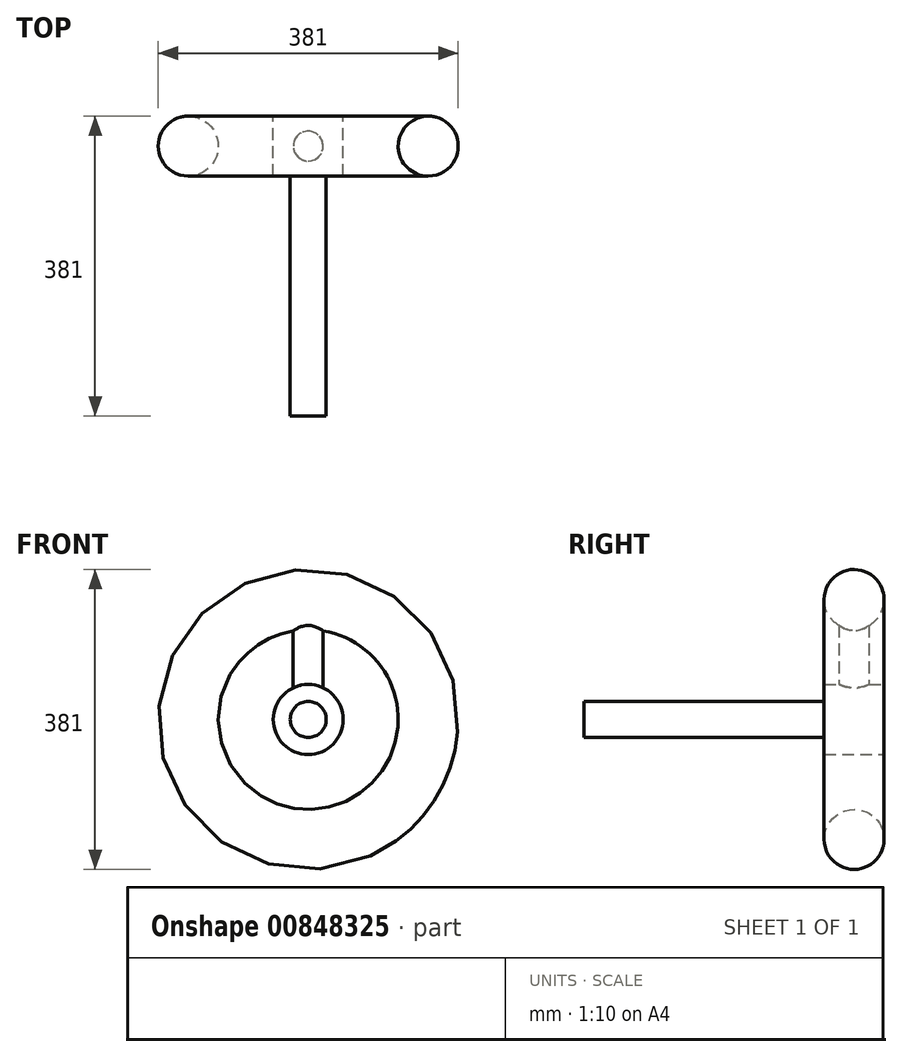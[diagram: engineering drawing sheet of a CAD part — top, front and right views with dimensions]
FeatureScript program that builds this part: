
annotation { "Feature Type Name" : "Feature", "Feature Type Description" : "" }
export const myFeature = defineFeature(function(context is Context, id is Id, definition is map)
    precondition{}
    {
        {
            var Q0;
            Q0=qCreatedBy(makeId("Right.planeOp"),FACE);
            var sketch = newSketch(context, id + "F0", { "sketchPlane" : qUnion([Q0])});
            skCircle(sketch, "E0", {"center": v(0, 152.4) * mm, "radius": 38.1 * mm});
            skLineSegment(sketch, "E1", {"start": v(-136.6, 0) * mm, "end": v(132.64, 0) * mm});
            skSolve(sketch);
        }
        {
            var Q0;
            Q0=makeQuery(id+"F0.imprint","IMPRINT",FACE,{"disambiguationData":[TD([[makeQuery(id+"F0.imprint","IMPRINT",EDGE,{"derivedFrom":sQuery(id+"F0.wireOp",EDGE,"E0")}),1.0]])]});
            var Q1;
            Q1=sQuery(id+"F0.wireOp",EDGE,"E1");
            revolve(context, id + "F1", {"surfaceOperationType" : NewSurfaceOperationType.NEW, "entities" : qUnion([Q0]), "axis" : qUnion([Q1]), "revolveType" : RevolveType.FULL});
        }
        {
            var Q0;
            Q0=qCreatedBy(makeId("Front.planeOp"),FACE);
            cPlane(context, id + "F2", {"entities" : qUnion([Q0]), "cplaneType" : CPlaneType.OFFSET, "offset" : 38.1 * mm, "oppositeDirection" : true, "width" : 152.4 * mm, "height" : 152.4 * mm});
        }
        {
            var Q0;
            Q0=qCreatedBy(id+"F2.planeOp",FACE);
            var sketch = newSketch(context, id + "F3", { "sketchPlane" : qUnion([Q0])});
            skCircle(sketch, "E2", {"center": v(0, 0) * mm, "radius": 44.45 * mm});
            skSolve(sketch);
        }
        {
            var Q0;
            Q0=makeQuery(id+"F3.imprint","IMPRINT",FACE,{"disambiguationData":[TD([[makeQuery(id+"F3.imprint","IMPRINT",EDGE,{"derivedFrom":sQuery(id+"F3.wireOp",EDGE,"E2")}),1.0]])]});
            extrude(context, id + "F4", {"entities" : qUnion([Q0]), "depth" : 76.2 * mm, "offsetDistance" : 25.4 * mm});
        }
        {
            var Q0;
            Q0=qCreatedBy(makeId("Top.planeOp"),FACE);
            cPlane(context, id + "F5", {"entities" : qUnion([Q0]), "cplaneType" : CPlaneType.OFFSET, "offset" : 38.1 * mm, "width" : 152.4 * mm, "height" : 152.4 * mm});
        }
        {
            var Q0;
            Q0=qCreatedBy(id+"F5.planeOp",FACE);
            var sketch = newSketch(context, id + "F6", { "sketchPlane" : qUnion([Q0])});
            skCircle(sketch, "E3", {"center": v(0, 0) * mm, "radius": 19.05 * mm});
            skSolve(sketch);
        }
        {
            var Q0;
            Q0 = qSketchRegion(id + "F6", true);
            var Q1;
            Q1=makeQuery(id+"F1.opRevolve","SWEPT_FACE",FACE,{"disambiguationData":[OSD([sQuery(id+"F0.wireOp",EDGE,"E0")])]});
            extrude(context, id + "F7", {"entities" : qUnion([Q0]), "operationType" : NewBodyOperationType.ADD, "endBound" : BoundingType.UP_TO_SURFACE, "depth" : 25.4 * mm, "endBoundEntityFace" : qUnion([Q1]), "offsetDistance" : 25.4 * mm});
        }
        {
            var Q0;
            Q0=makeQuery(id+"F4.opExtrude","CAP_FACE",FACE,{"disambiguationData":[OSD([sQuery(id+"F3.wireOp",EDGE,"E2")])],"isStart":false});
            var sketch = newSketch(context, id + "F8", { "sketchPlane" : qUnion([Q0])});
            skCircle(sketch, "E4", {"center": v(0, 0) * mm, "radius": 22.86 * mm});
            skSolve(sketch);
        }
        {
            var Q0;
            Q0=makeQuery(id+"F8.imprint","IMPRINT",FACE,{"disambiguationData":[TD([[makeQuery(id+"F8.imprint","IMPRINT",EDGE,{"derivedFrom":sQuery(id+"F8.wireOp",EDGE,"E4")}),1.0]])]});
            extrude(context, id + "F9", {"entities" : qUnion([Q0]), "operationType" : NewBodyOperationType.ADD, "depth" : 304.8 * mm, "offsetDistance" : 25.4 * mm});
        }
    });
